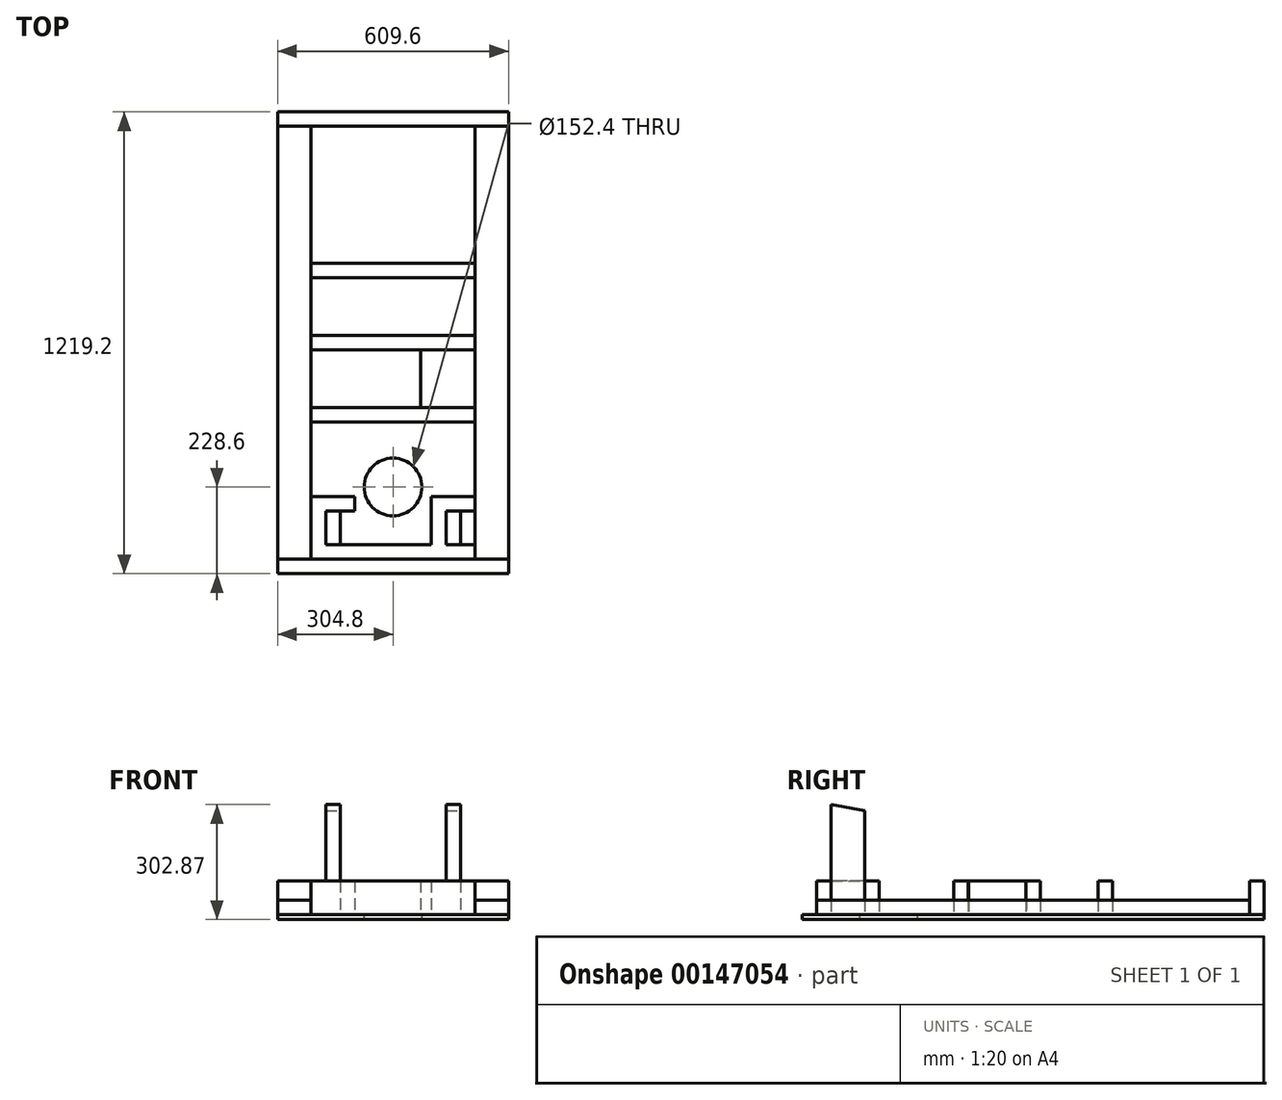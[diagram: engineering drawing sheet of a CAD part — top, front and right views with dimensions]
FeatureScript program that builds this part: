
annotation { "Feature Type Name" : "Feature", "Feature Type Description" : "" }
export const myFeature = defineFeature(function(context is Context, id is Id, definition is map)
    precondition{}
    {
        {
            var Q0;
            Q0=qCreatedBy(makeId("Top.planeOp"),FACE);
            var sketch = newSketch(context, id + "F0", { "sketchPlane" : qUnion([Q0])});
            skLineSegment(sketch, "E0", {"start": v(0, 0) * mm, "end": v(609.6, 0) * mm});
            skLineSegment(sketch, "E1", {"start": v(609.6, 0) * mm, "end": v(609.6, -38.1) * mm});
            skLineSegment(sketch, "E2", {"start": v(609.6, -38.1) * mm, "end": v(0, -38.1) * mm});
            skLineSegment(sketch, "E3", {"start": v(0, -38.1) * mm, "end": v(0, 0) * mm});
            skSolve(sketch);
        }
        {
            var Q0;
            Q0=makeQuery(id+"F0.imprint","IMPRINT",FACE,{"disambiguationData":[TD([[makeQuery(id+"F0.imprint","IMPRINT",EDGE,{"derivedFrom":sQuery(id+"F0.wireOp",EDGE,"E0")}),-1.0]])]});
            extrude(context, id + "F1", {"entities" : qUnion([Q0]), "depth" : 88.9 * mm});
        }
        {
            var Q0;
            Q0=qCreatedBy(makeId("Top.planeOp"),FACE);
            var sketch = newSketch(context, id + "F2", { "sketchPlane" : qUnion([Q0])});
            skLineSegment(sketch, "E4", {"start": v(0, -38.1) * mm, "end": v(0, -1181.1) * mm});
            skLineSegment(sketch, "E5", {"start": v(0, -1181.1) * mm, "end": v(88.9, -1181.1) * mm});
            skLineSegment(sketch, "E6", {"start": v(88.9, -1181.1) * mm, "end": v(88.9, -38.1) * mm});
            skLineSegment(sketch, "E7", {"start": v(88.9, -38.1) * mm, "end": v(0, -38.1) * mm});
            skLineSegment(sketch, "E8", {"start": v(520.7, -1181.1) * mm, "end": v(609.6, -1181.1) * mm});
            skPoint(sketch, "E8.endSnap0", {"position": v(304.8, -1181.1) * mm});
            skLineSegment(sketch, "E9", {"start": v(609.6, -1181.1) * mm, "end": v(609.6, -38.1) * mm});
            skLineSegment(sketch, "E10", {"start": v(609.6, -38.1) * mm, "end": v(520.7, -38.1) * mm});
            skLineSegment(sketch, "E11", {"start": v(520.7, -38.1) * mm, "end": v(520.7, -1181.1) * mm});
            skSolve(sketch);
        }
        {
            var Q0;
            Q0 = qSketchRegion(id + "F2", true);
            extrude(context, id + "F3", {"entities" : qUnion([Q0]), "depth" : 38.1 * mm});
        }
        {
            var Q0;
            Q0=qCreatedBy(makeId("Top.planeOp"),FACE);
            var sketch = newSketch(context, id + "F4", { "sketchPlane" : qUnion([Q0])});
            skLineSegment(sketch, "E12", {"start": v(88.9, -1181.1) * mm, "end": v(520.7, -1181.1) * mm});
            skLineSegment(sketch, "E13", {"start": v(520.7, -1181.1) * mm, "end": v(520.7, -1143) * mm});
            skLineSegment(sketch, "E14", {"start": v(520.7, -1143) * mm, "end": v(88.9, -1143) * mm});
            skLineSegment(sketch, "E15", {"start": v(88.9, -1143) * mm, "end": v(88.9, -1181.1) * mm});
            skLineSegment(sketch, "E16.bottom", {"start": v(88.9, -1143) * mm, "end": v(127, -1143) * mm});
            skLineSegment(sketch, "E16.top", {"start": v(88.9, -1054.1) * mm, "end": v(127, -1054.1) * mm});
            skLineSegment(sketch, "E16.left", {"start": v(88.9, -1143) * mm, "end": v(88.9, -1054.1) * mm});
            skLineSegment(sketch, "E16.right", {"start": v(127, -1143) * mm, "end": v(127, -1054.1) * mm});
            skLineSegment(sketch, "E17.bottom", {"start": v(88.9, -1054.1) * mm, "end": v(203.2, -1054.1) * mm});
            skLineSegment(sketch, "E17.top", {"start": v(88.9, -1016) * mm, "end": v(203.2, -1016) * mm});
            skLineSegment(sketch, "E17.left", {"start": v(88.9, -1054.1) * mm, "end": v(88.9, -1016) * mm});
            skLineSegment(sketch, "E17.right", {"start": v(203.2, -1054.1) * mm, "end": v(203.2, -1016) * mm});
            skLineSegment(sketch, "E18.bottom", {"start": v(203.2, -1054.1) * mm, "end": v(165.1, -1054.1) * mm});
            skLineSegment(sketch, "E18.top", {"start": v(203.2, -1143) * mm, "end": v(165.1, -1143) * mm});
            skLineSegment(sketch, "E18.left", {"start": v(203.2, -1054.1) * mm, "end": v(203.2, -1143) * mm});
            skLineSegment(sketch, "E18.right", {"start": v(165.1, -1054.1) * mm, "end": v(165.1, -1143) * mm});
            skLineSegment(sketch, "E19", {"start": v(304.8, -1143) * mm, "end": v(304.8, -1083.87) * mm});
            skPoint(sketch, "E19.endSnap0", {"position": v(304.8, -1143) * mm});
            skLineSegment(sketch, "E20.MirrorCS", {"start": v(520.7, -1143) * mm, "end": v(520.7, -1181.1) * mm});
            skLineSegment(sketch, "E21.MirrorCS", {"start": v(520.7, -1054.1) * mm, "end": v(482.6, -1054.1) * mm});
            skLineSegment(sketch, "E22.MirrorCS", {"start": v(406.4, -1143) * mm, "end": v(444.5, -1143) * mm});
            skLineSegment(sketch, "E23.MirrorCS", {"start": v(406.4, -1054.1) * mm, "end": v(444.5, -1054.1) * mm});
            skLineSegment(sketch, "E24.MirrorCS", {"start": v(88.9, -1143) * mm, "end": v(520.7, -1143) * mm});
            skLineSegment(sketch, "E25.MirrorCS", {"start": v(520.7, -1016) * mm, "end": v(406.4, -1016) * mm});
            skLineSegment(sketch, "E26.MirrorCS", {"start": v(520.7, -1054.1) * mm, "end": v(520.7, -1016) * mm});
            skLineSegment(sketch, "E27.MirrorCS", {"start": v(520.7, -1143) * mm, "end": v(482.6, -1143) * mm});
            skLineSegment(sketch, "E28.MirrorCS", {"start": v(520.7, -1054.1) * mm, "end": v(406.4, -1054.1) * mm});
            skLineSegment(sketch, "E29.MirrorCS", {"start": v(406.4, -1054.1) * mm, "end": v(406.4, -1016) * mm});
            skLineSegment(sketch, "E30.MirrorCS", {"start": v(406.4, -1054.1) * mm, "end": v(406.4, -1143) * mm});
            skLineSegment(sketch, "E31.MirrorCS", {"start": v(482.6, -1143) * mm, "end": v(482.6, -1054.1) * mm});
            skLineSegment(sketch, "E32.MirrorCS", {"start": v(444.5, -1054.1) * mm, "end": v(444.5, -1143) * mm});
            skLineSegment(sketch, "E33.MirrorCS", {"start": v(520.7, -1143) * mm, "end": v(520.7, -1054.1) * mm});
            skSolve(sketch);
        }
        {
            var Q0;
            Q0=makeQuery(id+"F4.imprint","IMPRINT",FACE,{"disambiguationData":[TD([[makeQuery(id+"F4.imprint","IMPRINT",EDGE,{"derivedFrom":sQuery(id+"F4.wireOp",EDGE,"E25.MirrorCS")}),1.0]])]});
            var Q1;
            Q1=makeQuery(id+"F4.imprint","IMPRINT",FACE,{"disambiguationData":[TD([[makeQuery(id+"F4.imprint","IMPRINT",EDGE,{"derivedFrom":sQuery(id+"F4.wireOp",EDGE,"E12")}),1.0]])]});
            var Q2;
            Q2=makeQuery(id+"F4.imprint","IMPRINT",FACE,{"disambiguationData":[TD([[makeQuery(id+"F4.imprint","IMPRINT",EDGE,{"derivedFrom":sQuery(id+"F4.wireOp",EDGE,"E17.top")}),-1.0]])]});
            var Q3;
            {var subQ0=sQuery(id+"F4.wireOp",EDGE,"E16.left");Q3=makeQuery(id+"F4.imprint","IMPRINT",FACE,{"disambiguationData":[TD([[makeQuery(id+"F4.imprint","IMPRINT",EDGE,{"derivedFrom":subQ0}),-1.0]])]});}
            var Q4;
            Q4=makeQuery(id+"F4.imprint","IMPRINT",FACE,{"disambiguationData":[TD([[makeQuery(id+"F4.imprint","IMPRINT",EDGE,{"derivedFrom":sQuery(id+"F4.wireOp",EDGE,"E18.bottom")}),1.0]])]});
            var Q5;
            {var subQ0=sQuery(id+"F4.wireOp",EDGE,"E30.MirrorCS");Q5=makeQuery(id+"F4.imprint","IMPRINT",FACE,{"disambiguationData":[TD([[makeQuery(id+"F4.imprint","IMPRINT",EDGE,{"derivedFrom":subQ0}),1.0]])]});}
            var Q6;
            Q6=makeQuery(id+"F4.imprint","IMPRINT",FACE,{"disambiguationData":[TD([[makeQuery(id+"F4.imprint","IMPRINT",EDGE,{"derivedFrom":sQuery(id+"F4.wireOp",EDGE,"E27.MirrorCS")}),-1.0]])]});
            extrude(context, id + "F5", {"entities" : qUnion([Q0, Q1, Q2, Q3, Q4, Q5, Q6]), "depth" : 88.9 * mm});
        }
        {
            var Q0;
            Q0=makeQuery(id+"F5.opExtrude","CAP_FACE",FACE,{"disambiguationData":[OSD([sQuery(id+"F4.wireOp",EDGE,"E12"),sQuery(id+"F4.wireOp",EDGE,"E15"),sQuery(id+"F4.wireOp",EDGE,"E16.left"),sQuery(id+"F4.wireOp",EDGE,"E16.right"),sQuery(id+"F4.wireOp",EDGE,"E17.bottom"),sQuery(id+"F4.wireOp",EDGE,"E17.top"),sQuery(id+"F4.wireOp",EDGE,"E17.left"),sQuery(id+"F4.wireOp",EDGE,"E17.right"),sQuery(id+"F4.wireOp",EDGE,"E18.left"),sQuery(id+"F4.wireOp",EDGE,"E18.right"),sQuery(id+"F4.wireOp",EDGE,"E20.MirrorCS"),sQuery(id+"F4.wireOp",EDGE,"E24.MirrorCS"),sQuery(id+"F4.wireOp",EDGE,"E25.MirrorCS"),sQuery(id+"F4.wireOp",EDGE,"E26.MirrorCS"),sQuery(id+"F4.wireOp",EDGE,"E28.MirrorCS"),sQuery(id+"F4.wireOp",EDGE,"E29.MirrorCS"),sQuery(id+"F4.wireOp",EDGE,"E30.MirrorCS"),sQuery(id+"F4.wireOp",EDGE,"E31.MirrorCS"),sQuery(id+"F4.wireOp",EDGE,"E32.MirrorCS"),sQuery(id+"F4.wireOp",EDGE,"E33.MirrorCS")])],"isStart":true});
            var sketch = newSketch(context, id + "F6", { "sketchPlane" : qUnion([Q0])});
            skLineSegment(sketch, "E34.bottom", {"start": v(482.6, 1054.1) * mm, "end": v(444.5, 1054.1) * mm});
            skLineSegment(sketch, "E34.top", {"start": v(482.6, 1143) * mm, "end": v(444.5, 1143) * mm});
            skLineSegment(sketch, "E34.left", {"start": v(482.6, 1054.1) * mm, "end": v(482.6, 1143) * mm});
            skLineSegment(sketch, "E34.right", {"start": v(444.5, 1054.1) * mm, "end": v(444.5, 1143) * mm});
            skLineSegment(sketch, "E35.bottom", {"start": v(165.1, 1143) * mm, "end": v(127, 1143) * mm});
            skLineSegment(sketch, "E35.top", {"start": v(165.1, 1054.1) * mm, "end": v(127, 1054.1) * mm});
            skLineSegment(sketch, "E35.left", {"start": v(165.1, 1143) * mm, "end": v(165.1, 1054.1) * mm});
            skLineSegment(sketch, "E35.right", {"start": v(127, 1143) * mm, "end": v(127, 1054.1) * mm});
            skSolve(sketch);
        }
        {
            var Q0;
            Q0 = qSketchRegion(id + "F6", true);
            extrude(context, id + "F7", {"entities" : qUnion([Q0]), "operationType" : NewBodyOperationType.ADD, "oppositeDirection" : true, "depth" : 290.17 * mm});
        }
        {
            var Q0;
            Q0=makeQuery(id+"F7.opExtrude","SWEPT_FACE",FACE,{"disambiguationData":[OSD([sQuery(id+"F6.wireOp",EDGE,"E34.left")])]});
            var sketch = newSketch(context, id + "F8", { "sketchPlane" : qUnion([Q0])});
            skLineSegment(sketch, "E36", {"start": v(-1054.1, 290.17) * mm, "end": v(-1054.1, 273.99) * mm});
            skLineSegment(sketch, "E37", {"start": v(-1054.1, 273.99) * mm, "end": v(-1143, 290.17) * mm});
            skLineSegment(sketch, "E38", {"start": v(-1143, 290.17) * mm, "end": v(-1054.1, 290.17) * mm});
            skSolve(sketch);
        }
        {
            var Q0;
            Q0 = qSketchRegion(id + "F8", true);
            extrude(context, id + "F9", {"entities" : qUnion([Q0]), "operationType" : NewBodyOperationType.REMOVE, "endBound" : BoundingType.THROUGH_ALL, "oppositeDirection" : true, "depth" : 25.4 * mm});
        }
        {
            var Q0;
            Q0=makeQuery(id+"F1.opExtrude","CAP_FACE",FACE,{"disambiguationData":[OSD([sQuery(id+"F0.wireOp",EDGE,"E0"),sQuery(id+"F0.wireOp",EDGE,"E1"),sQuery(id+"F0.wireOp",EDGE,"E2"),sQuery(id+"F0.wireOp",EDGE,"E3")])],"isStart":true});
            var sketch = newSketch(context, id + "F10", { "sketchPlane" : qUnion([Q0])});
            skLineSegment(sketch, "E39.bottom", {"start": v(0, 0) * mm, "end": v(609.6, 0) * mm});
            skLineSegment(sketch, "E39.top", {"start": v(0, 1219.2) * mm, "end": v(609.6, 1219.2) * mm});
            skLineSegment(sketch, "E39.left", {"start": v(0, 0) * mm, "end": v(0, 1219.2) * mm});
            skLineSegment(sketch, "E39.right", {"start": v(609.6, 0) * mm, "end": v(609.6, 1219.2) * mm});
            skCircle(sketch, "E40", {"center": v(304.8, 990.6) * mm, "radius": 76.2 * mm});
            skSolve(sketch);
        }
        {
            var Q0;
            Q0 = qSketchRegion(id + "F10", true);
            extrude(context, id + "F11", {"entities" : qUnion([Q0]), "depth" : 12.7 * mm});
        }
        {
            var Q0;
            Q0=makeQuery(id+"F11.opExtrude","CAP_FACE",FACE,{"disambiguationData":[OSD([sQuery(id+"F10.wireOp",EDGE,"E39.bottom"),sQuery(id+"F10.wireOp",EDGE,"E39.top"),sQuery(id+"F10.wireOp",EDGE,"E39.left"),sQuery(id+"F10.wireOp",EDGE,"E39.right"),sQuery(id+"F10.wireOp",EDGE,"E40")])],"isStart":true});
            var sketch = newSketch(context, id + "F12", { "sketchPlane" : qUnion([Q0])});
            skPoint(sketch, "E41.endSnap0", {"position": v(609.6, -609.6) * mm});
            skLineSegment(sketch, "E42.0", {"start": v(520.7, -590.55) * mm, "end": v(88.9, -590.55) * mm});
            skLineSegment(sketch, "E43.0", {"start": v(520.7, -628.65) * mm, "end": v(88.9, -628.65) * mm});
            skPoint(sketch, "E41.start.orphan", {"position": v(609.6, -609.6) * mm});
            skPoint(sketch, "E44.start.orphan", {"position": v(520.7, -609.6) * mm});
            skLineSegment(sketch, "E45", {"start": v(88.9, -590.55) * mm, "end": v(88.9, -438.15) * mm});
            skLineSegment(sketch, "E46", {"start": v(88.9, -590.55) * mm, "end": v(88.9, -628.65) * mm});
            skLineSegment(sketch, "E47", {"start": v(88.9, -628.65) * mm, "end": v(88.9, -590.55) * mm});
            skLineSegment(sketch, "E48", {"start": v(520.7, -590.55) * mm, "end": v(520.7, -628.65) * mm});
            skLineSegment(sketch, "E49.bottom", {"start": v(88.9, -438.15) * mm, "end": v(520.7, -438.15) * mm});
            skLineSegment(sketch, "E49.top", {"start": v(88.9, -400.05) * mm, "end": v(520.7, -400.05) * mm});
            skLineSegment(sketch, "E49.left", {"start": v(88.9, -438.15) * mm, "end": v(88.9, -400.05) * mm});
            skLineSegment(sketch, "E49.right", {"start": v(520.7, -438.15) * mm, "end": v(520.7, -400.05) * mm});
            skLineSegment(sketch, "E50.bottom", {"start": v(88.9, -781.05) * mm, "end": v(520.7, -781.05) * mm});
            skLineSegment(sketch, "E50.top", {"start": v(88.9, -819.15) * mm, "end": v(520.7, -819.15) * mm});
            skLineSegment(sketch, "E50.left", {"start": v(88.9, -781.05) * mm, "end": v(88.9, -819.15) * mm});
            skLineSegment(sketch, "E50.right", {"start": v(520.7, -781.05) * mm, "end": v(520.7, -819.15) * mm});
            skSolve(sketch);
        }
        {
            var Q0;
            Q0 = qSketchRegion(id + "F12", true);
            extrude(context, id + "F13", {"entities" : qUnion([Q0]), "depth" : 88.9 * mm});
        }
        {
            var Q0;
            Q0=makeQuery(id+"F11.opExtrude","CAP_FACE",FACE,{"disambiguationData":[OSD([sQuery(id+"F10.wireOp",EDGE,"E39.bottom"),sQuery(id+"F10.wireOp",EDGE,"E39.top"),sQuery(id+"F10.wireOp",EDGE,"E39.left"),sQuery(id+"F10.wireOp",EDGE,"E39.right"),sQuery(id+"F10.wireOp",EDGE,"E40")])],"isStart":true});
            var sketch = newSketch(context, id + "F14", { "sketchPlane" : qUnion([Q0])});
            skLineSegment(sketch, "E51", {"start": v(88.1, -780.57) * mm, "end": v(378.27, -780.57) * mm});
            skLineSegment(sketch, "E52", {"start": v(378.27, -780.57) * mm, "end": v(378.27, -628.17) * mm});
            skLineSegment(sketch, "E53", {"start": v(378.27, -628.17) * mm, "end": v(88.1, -628.17) * mm});
            skLineSegment(sketch, "E54", {"start": v(88.1, -628.17) * mm, "end": v(88.1, -780.57) * mm});
            skSolve(sketch);
        }
        {
            var Q0;
            Q0 = qSketchRegion(id + "F14", true);
            extrude(context, id + "F15", {"entities" : qUnion([Q0]), "depth" : 88.9 * mm});
        }
    });
